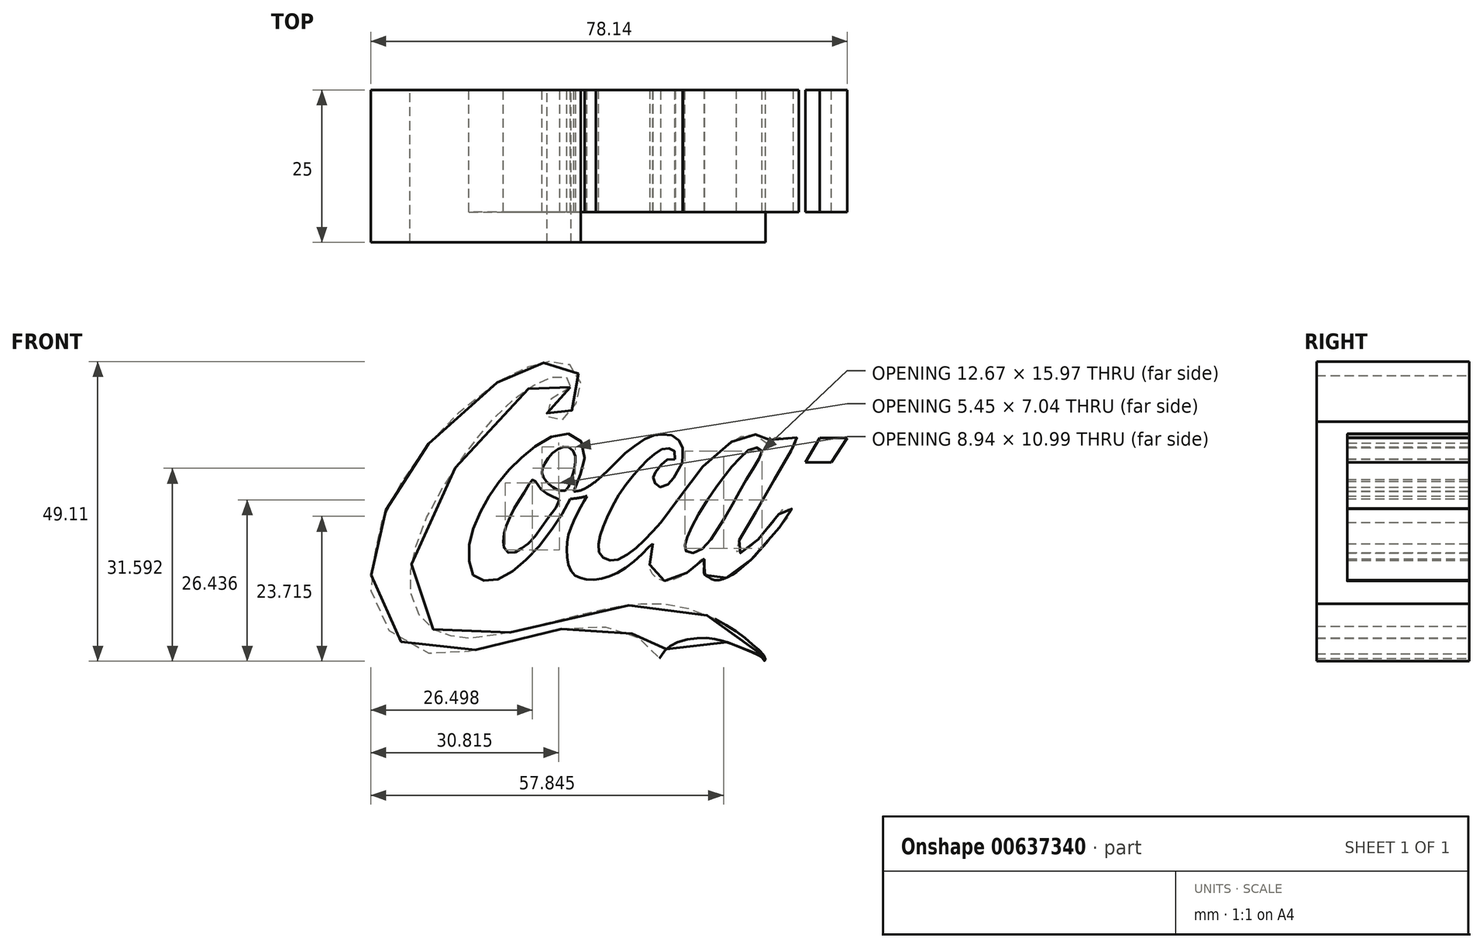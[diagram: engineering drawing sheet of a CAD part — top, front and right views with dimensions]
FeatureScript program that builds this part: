
annotation { "Feature Type Name" : "Feature", "Feature Type Description" : "" }
export const myFeature = defineFeature(function(context is Context, id is Id, definition is map)
    precondition{}
    {
        {
            var Q0;
            Q0=qCreatedBy(makeId("Front.planeOp"),FACE);
            var sketch = newSketch(context, id + "F0", { "sketchPlane" : qUnion([Q0])});
            skFitSpline(sketch, "E0", {"points": [v(-42.27, 50.75) * mm, v(-44.4, 49.85) * mm, v(-45.43, 48.84) * mm, v(-45.92, 47.9) * mm, v(-46.12, 46.72) * mm, v(-46, 45.7) * mm, v(-45.25, 45.2) * mm, v(-44, 45.25) * mm, v(-42.76, 46.12) * mm, v(-41.77, 47.37) * mm, v(-40.95, 48.92) * mm, v(-40.61, 50.39) * mm, v(-40.68, 52.13) * mm, v(-41.26, 53.5) * mm, v(-42.66, 54.58) * mm, v(-44.13, 54.95) * mm, v(-45.77, 54.95) * mm, v(-47.3, 54.64) * mm, v(-49, 54.15) * mm, v(-51.37, 53.13) * mm, v(-56.04, 50.4) * mm, v(-63.95, 43.3) * mm, v(-67.27, 39.2) * mm, v(-71.38, 32.82) * mm, v(-73.65, 27.39) * mm, v(-74.6, 22.16) * mm, v(-75, 19.09) * mm, v(-74.16, 14.13) * mm, v(-68.65, 8.18) * mm, v(-62.57, 7.1) * mm, v(-56.53, 8.04) * mm, v(-47.9, 10.27) * mm, v(-40.77, 11.56) * mm, v(-34.97, 11.27) * mm, v(-31.17, 9.78) * mm, v(-27.96, 6.82) * mm, v(-27.7, 6.35) * mm, v(-27.27, 6.95) * mm, v(-25.27, 8.76) * mm, v(-20.37, 9.68) * mm, v(-16.41, 8.93) * mm, v(-11.6, 6.9) * mm, v(-10.77, 6.33) * mm, v(-10.38, 5.9) * mm, v(-10.34, 6.36) * mm, v(-11.82, 8.1) * mm, v(-16.6, 11.71) * mm, v(-24.49, 14.86) * mm, v(-30.73, 15.2) * mm, v(-38.32, 14.02) * mm, v(-57.16, 9.7) * mm, v(-61.95, 10.04) * mm, v(-65.5, 11.6) * mm, v(-68.28, 16.26) * mm, v(-68.2, 22.25) * mm, v(-64.73, 31.66) * mm, v(-54.91, 45.6) * mm, v(-48.44, 51) * mm, v(-44.45, 52.63) * mm, v(-42.61, 52.22) * mm, v(-42.27, 50.75) * mm]});
            skSolve(sketch);
        }
        {
            var Q0;
            Q0=qCreatedBy(makeId("Front.planeOp"),FACE);
            var sketch = newSketch(context, id + "F1", { "sketchPlane" : qUnion([Q0])});
            skFitSpline(sketch, "E1", {"points": [v(-39.94, 40.1) * mm, v(-41.08, 42.55) * mm, v(-43.29, 43.15) * mm, v(-46.33, 42.22) * mm, v(-49.1, 40.26) * mm, v(-51.31, 38.28) * mm, v(-53.27, 36.13) * mm, v(-54.92, 33.95) * mm, v(-56.42, 31.58) * mm, v(-57.9, 28.36) * mm, v(-58.82, 25.68) * mm, v(-58.9, 23.24) * mm, v(-58.66, 20.72) * mm, v(-57.59, 19.49) * mm, v(-56.1, 19.07) * mm, v(-54.1, 19.33) * mm, v(-51.72, 20.64) * mm, v(-49.46, 22.58) * mm, v(-46.9, 25.36) * mm, v(-44.33, 28.97) * mm, v(-43.05, 31.05) * mm, v(-41.42, 34.38) * mm, v(-40.39, 37.26) * mm, v(-39.94, 40.1) * mm]});
            skFitSpline(sketch, "E2", {"points": [v(-41.48, 39.45) * mm, v(-42.04, 40.61) * mm, v(-43.05, 41.01) * mm, v(-44.35, 40.63) * mm, v(-45.6, 39.53) * mm, v(-46.48, 38.25) * mm, v(-46.92, 37.18) * mm, v(-46.83, 36.36) * mm, v(-46.5, 35.63) * mm, v(-45.96, 35.08) * mm, v(-45.41, 34.58) * mm, v(-44.7, 34.1) * mm, v(-44.02, 33.9) * mm, v(-43.31, 33.78) * mm, v(-42.72, 34.26) * mm, v(-42.3, 35.25) * mm, v(-42, 36.18) * mm, v(-41.7, 37.15) * mm, v(-41.48, 38.2) * mm, v(-41.48, 39.45) * mm]});
            skFitSpline(sketch, "E3", {"points": [v(-44.05, 32.37) * mm, v(-45.07, 32.82) * mm, v(-46.19, 33.37) * mm, v(-47.27, 34.26) * mm, v(-48.27, 35.63) * mm, v(-48.43, 35.63) * mm, v(-48.7, 35.45) * mm, v(-49.4, 34.26) * mm, v(-50.53, 32.44) * mm, v(-51.67, 30.6) * mm, v(-52.55, 28.62) * mm, v(-53.06, 27.15) * mm, v(-53.3, 25.35) * mm, v(-53.2, 24.54) * mm, v(-52.62, 23.73) * mm, v(-51.43, 23.7) * mm, v(-50.28, 24.35) * mm, v(-49.02, 25.3) * mm, v(-47.22, 27.56) * mm, v(-45.3, 30.14) * mm, v(-44.05, 32.37) * mm]});
            skFitSpline(sketch, "E4", {"points": [v(-41.73, 33.7) * mm, v(-40.13, 34.07) * mm, v(-38.96, 34.75) * mm, v(-37.53, 35.7) * mm, v(-35.07, 36.94) * mm, v(-35.05, 36.94) * mm], "startDerivative": vector(10.3, 0.82) * mm, "endDerivative": vector(1.23, -0.24) * mm});
            skFitSpline(sketch, "E5", {"points": [v(-42.3, 32.48) * mm, v(-41.27, 32.58) * mm, v(-39.57, 32.96) * mm, v(-38.12, 33.65) * mm, v(-36.34, 34.6) * mm], "startDerivative": vector(4.88, 0.37) * mm, "endDerivative": vector(6.4, 3.39) * mm});
            skLineSegment(sketch, "E6", {"start": v(-35.05, 36.94) * mm, "end": v(-36.34, 34.6) * mm});
            skSolve(sketch);
        }
        {
            var Q0;
            Q0=qCreatedBy(makeId("Front.planeOp"),FACE);
            var sketch = newSketch(context, id + "F2", { "sketchPlane" : qUnion([Q0])});
            skFitSpline(sketch, "E7", {"points": [v(-25.18, 38.95) * mm, v(-25.18, 40.22) * mm, v(-25.78, 40.64) * mm, v(-26.33, 40.8) * mm, v(-27.32, 40.6) * mm, v(-28.5, 39.81) * mm, v(-29.6, 38.9) * mm, v(-30.68, 37.74) * mm, v(-32, 36.28) * mm, v(-33.7, 34.11) * mm, v(-35.13, 31.7) * mm, v(-36.33, 29.27) * mm, v(-37.02, 27.67) * mm, v(-37.46, 26.3) * mm, v(-37.68, 24.93) * mm, v(-37.6, 23.83) * mm, v(-37.17, 23.05) * mm, v(-36.56, 22.64) * mm, v(-35.46, 22.35) * mm, v(-34.37, 22.58) * mm, v(-32.57, 23.59) * mm, v(-31.04, 24.84) * mm, v(-29.24, 26.63) * mm, v(-27.52, 28.54) * mm, v(-25.96, 29.88) * mm], "startDerivative": vector(6.47, 39.09) * mm, "endDerivative": vector(31.99, 26.85) * mm});
            skFitSpline(sketch, "E8", {"points": [v(-25.18, 38.95) * mm, v(-26.31, 38.95) * mm, v(-27.28, 38.23) * mm, v(-28.33, 36.84) * mm, v(-28.63, 36.27) * mm, v(-28.63, 35.49) * mm, v(-28.24, 34.82) * mm, v(-27.52, 34.4) * mm, v(-26.22, 34.94) * mm, v(-25.18, 36.18) * mm, v(-24.22, 37.92) * mm, v(-23.9, 38.52) * mm, v(-23.86, 39.9) * mm, v(-23.9, 40.92) * mm, v(-24.58, 42.2) * mm, v(-25.96, 43) * mm, v(-27.74, 43.02) * mm, v(-29.09, 42.74) * mm, v(-31.48, 41.35) * mm, v(-33.64, 39.63) * mm, v(-35.63, 37.61) * mm, v(-37.1, 36.23) * mm, v(-38.03, 35.4) * mm, v(-38.5, 34.97) * mm, v(-38.5, 34.96) * mm], "startDerivative": vector(-30.41, 3.75) * mm, "endDerivative": vector(-0.63, -2.47) * mm});
            skFitSpline(sketch, "E9", {"points": [v(-39.51, 33.1) * mm, v(-39.87, 32.46) * mm, v(-40.61, 31.15) * mm, v(-41.47, 29.39) * mm, v(-42.12, 28) * mm, v(-42.66, 26.25) * mm, v(-42.83, 24.6) * mm, v(-42.8, 22.74) * mm, v(-42.45, 21.22) * mm, v(-41.8, 20.13) * mm, v(-40.82, 19.63) * mm, v(-39.81, 19.28) * mm, v(-38.07, 19.28) * mm, v(-36.2, 19.66) * mm, v(-33.92, 20.74) * mm, v(-31.4, 22.6) * mm, v(-29.28, 24.72) * mm, v(-28.62, 25.26) * mm, v(-26.76, 26.8) * mm], "startDerivative": vector(-8.89, -16.07) * mm, "endDerivative": vector(32.58, 27.03) * mm});
            skLineSegment(sketch, "E10", {"start": v(-38.5, 34.97) * mm, "end": v(-39.51, 33.1) * mm});
            skLineSegment(sketch, "E11", {"start": v(-25.96, 29.88) * mm, "end": v(-26.76, 26.8) * mm});
            skSolve(sketch);
        }
        {
            var Q0;
            Q0=qCreatedBy(makeId("Front.planeOp"),FACE);
            var sketch = newSketch(context, id + "F3", { "sketchPlane" : qUnion([Q0])});
            skFitSpline(sketch, "E12", {"points": [v(-27.69, 28.29) * mm, v(-26.07, 30.48) * mm, v(-24.28, 32.86) * mm, v(-21.24, 37) * mm, v(-18.24, 40) * mm, v(-14.59, 42.58) * mm, v(-13, 43.05) * mm, v(-11.5, 42.87) * mm, v(-10.16, 41.64) * mm, v(-9.92, 41.6) * mm, v(-9.5, 42.3) * mm, v(-8.34, 42.54) * mm, v(-5.04, 42.51) * mm, v(-4.9, 42.46) * mm, v(-4.8, 42.35) * mm, v(-5.25, 41.71) * mm, v(-6.36, 39.83) * mm, v(-8.2, 36.71) * mm, v(-9.92, 33.89) * mm, v(-12.34, 29.44) * mm, v(-14.11, 26.47) * mm, v(-15.08, 24.82) * mm, v(-15.1, 24.1) * mm, v(-14.9, 23.67) * mm, v(-14.14, 23.65) * mm, v(-12.85, 24.57) * mm, v(-11.6, 25.73) * mm, v(-9.65, 27.82) * mm, v(-7.8, 30.38) * mm, v(-7.47, 30.74) * mm, v(-7.38, 30.8) * mm, v(-7.29, 30.87) * mm, v(-5.98, 30.85) * mm, v(-5.9, 30.85) * mm, v(-5.84, 30.85) * mm, v(-5.78, 30.74) * mm, v(-7.31, 28.67) * mm, v(-11.54, 23.68) * mm, v(-13.96, 21.37) * mm, v(-16.44, 19.65) * mm, v(-18.77, 19.19) * mm, v(-19.95, 19.84) * mm, v(-20.29, 20.1) * mm, v(-20.36, 21.34) * mm, v(-20.33, 22.55) * mm, v(-20.4, 22.6) * mm, v(-20.66, 22.57) * mm, v(-21.37, 21.95) * mm, v(-22.98, 20.51) * mm, v(-24.9, 19.41) * mm, v(-26.48, 19.02) * mm, v(-27.9, 19.4) * mm, v(-29.12, 20.7) * mm, v(-29.21, 22.65) * mm, v(-28.91, 24.05) * mm, v(-28.76, 25.17) * mm, v(-28.84, 25.38) * mm], "startDerivative": vector(66.98, 91.98) * mm, "endDerivative": vector(-13.94, 23.08) * mm});
            skFitSpline(sketch, "E13", {"points": [v(-10.84, 40.31) * mm, v(-11.27, 40.77) * mm, v(-12.5, 40.8) * mm, v(-13.9, 39.73) * mm, v(-15.6, 37.97) * mm, v(-16.93, 36.37) * mm, v(-19.13, 33.33) * mm, v(-21.67, 29.26) * mm, v(-22.92, 26.73) * mm, v(-23.47, 25.28) * mm, v(-23.52, 24.44) * mm, v(-23.32, 23.87) * mm, v(-22.42, 23.6) * mm, v(-20.95, 24.1) * mm, v(-19.15, 25.97) * mm, v(-17.53, 28.51) * mm, v(-15.68, 31.63) * mm, v(-13.98, 34.73) * mm, v(-12.51, 37.13) * mm, v(-11.3, 39.18) * mm, v(-10.84, 40.31) * mm]});
            skLineSegment(sketch, "E14", {"start": v(-27.69, 28.29) * mm, "end": v(-28.76, 25.17) * mm});
            skSolve(sketch);
        }
        {
            var Q0;
            Q0=qCreatedBy(makeId("Front.planeOp"),FACE);
            var sketch = newSketch(context, id + "F4", { "sketchPlane" : qUnion([Q0])});
            skLineSegment(sketch, "E15", {"start": v(-1.42, 42.45) * mm, "end": v(-3.75, 38.44) * mm});
            skLineSegment(sketch, "E16", {"start": v(-3.75, 38.44) * mm, "end": v(0.5, 38.44) * mm});
            skLineSegment(sketch, "E17", {"start": v(-1.42, 42.45) * mm, "end": v(3.12, 42.45) * mm});
            skLineSegment(sketch, "E18", {"start": v(0.5, 38.44) * mm, "end": v(3.12, 42.45) * mm});
            skSolve(sketch);
        }
        {
            var Q0;
            Q0 = qSketchRegion(id + "F0", true);
            extrude(context, id + "F5", {"entities" : qUnion([Q0]), "depth" : 25 * mm, "offsetDistance" : 25 * mm});
        }
        {
            var Q0;
            Q0 = qSketchRegion(id + "F2", true);
            extrude(context, id + "F6", {"entities" : qUnion([Q0]), "depth" : 20 * mm, "offsetDistance" : 25 * mm});
        }
        {
            var Q0;
            Q0 = qSketchRegion(id + "F3", true);
            extrude(context, id + "F7", {"entities" : qUnion([Q0]), "operationType" : NewBodyOperationType.ADD, "depth" : 20 * mm, "offsetDistance" : 25 * mm});
        }
        {
            var Q0;
            Q0 = qSketchRegion(id + "F1", true);
            extrude(context, id + "F8", {"entities" : qUnion([Q0]), "operationType" : NewBodyOperationType.ADD, "depth" : 20 * mm, "offsetDistance" : 25 * mm});
        }
        {
            var Q0;
            Q0 = qSketchRegion(id + "F4", true);
            extrude(context, id + "F9", {"entities" : qUnion([Q0]), "depth" : 20 * mm, "offsetDistance" : 25 * mm});
        }
    });
